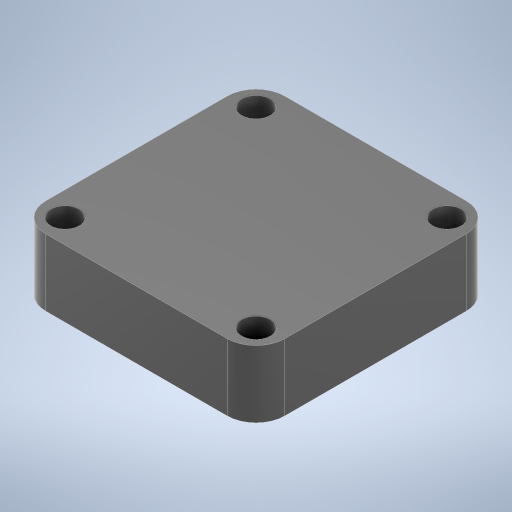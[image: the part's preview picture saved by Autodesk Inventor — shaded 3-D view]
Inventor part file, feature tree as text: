
AUTODESK INVENTOR PART (.ipt)
format: ipt  version: 2024.2 (Build 282272000, 272)  size: 226,816 bytes
history: native  units: mm
features: sketch x1, extrude x1, fillet x1, hole x1
ambient origin geometry x8: Origin, YZ Plane, XZ Plane, XY Plane, X Axis, Y Axis, Z Axis, Center Point
bodies: Solid1 (feature_tree)
feature tree (4):
  sketch  "Sketch1"  dims[d0=25.0mm d1=25.0mm d2=20.0mm d3=20.0mm d4=7.0mm d5=0.0mm d6=3.0mm d7=3.0mm d8=6.0mm d9=4.0mm d10=2.0mm d11=90.0deg d12=8.0mm d13=20.594885mm]
  extrude  "Extrusion1"  Depth=25.0mm
  fillet  "Fillet1"  Radius=20.0mm
  hole  "Hole1"  [1 undecoded]
note: 1 required parameter value undecoded (feature->parameter linkage not recoverable at this tier; creation-order binding heuristic only, values carry confidence <= 0.55)
